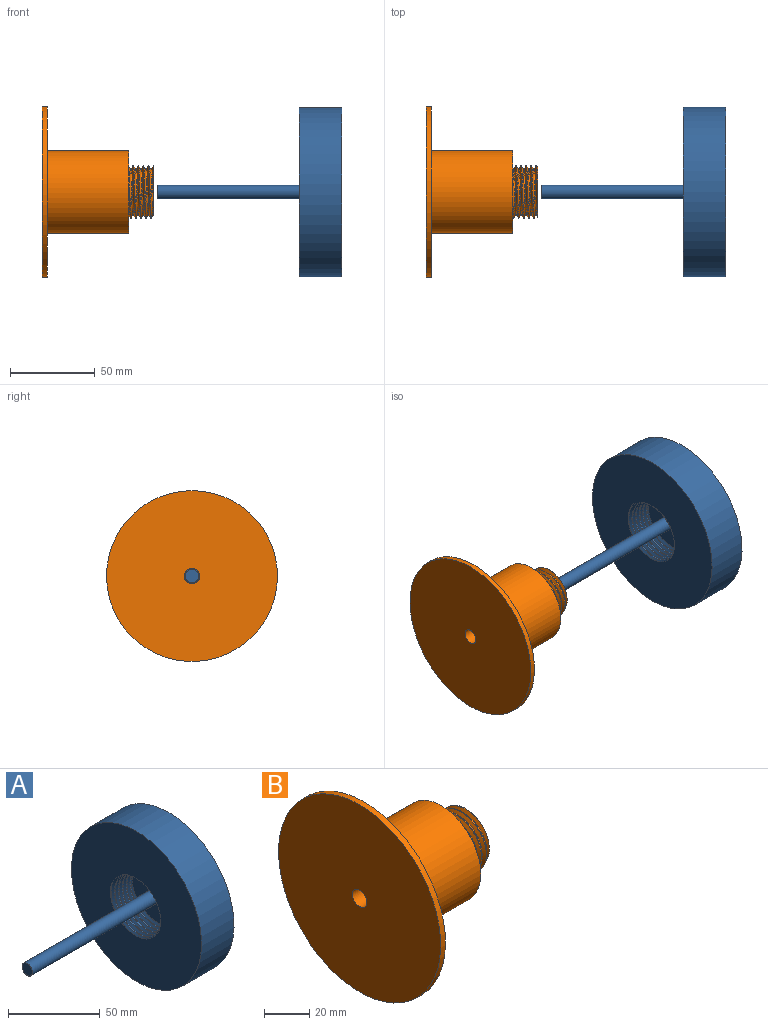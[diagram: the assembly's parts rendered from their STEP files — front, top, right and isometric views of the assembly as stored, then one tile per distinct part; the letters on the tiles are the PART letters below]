
ASSEMBLY  parts=2 mates=1
PART A: 10 faces, bbox 109.3x100.3x100.3 mm
  f0: plane 39.02x38.68mm, normal (-1,0,0), area 1111.3mm2, adj f5,f6,f7,f8,f9
  f1: plane 100.33x100.33mm, normal (-1,0,0), area 6692.4mm2, adj f4,f6,f7,f8,f9
  f2: plane 8x8mm, normal (-1,0,0), area 50.3mm2, adj f5
  f3: plane 100x100mm, normal (1,0,0), area 7854mm2, adj f4
  f4: cylinder r=50mm len=100mm, axis (-1,0,0), area 7854mm2, adj f1,f3
  f5: cylinder r=4mm len=100mm, axis (-1,0,0), area 2513.3mm2, adj f0,f2
  f6: bspline ~46.47x40.25mm, area 1214.5mm2, adj f0,f1,f8,f9
  f7: bspline ~46.47x40.25mm, area 1213.8mm2, adj f0,f1,f8,f9
  f8: bspline ~46.79x40.52mm, area 294mm2, adj f0,f1,f6,f7
  f9: cylinder r=18.5mm len=37mm, axis (1,0,0), area 450.2mm2, adj f0,f1,f6,f7
PART B: 11 faces, bbox 68x101.8x101.8 mm
  f0: cylinder r=15.5mm len=31mm, axis (-1,0,0), area 186.1mm2, adj f3,f4,f9,f10
  f1: plane 101x101mm, normal (-1,0,0), area 7948.2mm2, adj f2,f7
  f2: cylinder r=4.5mm len=66mm, axis (-1,0,0), area 1866.1mm2, adj f1,f3
  f3: plane 30.09x29.95mm, normal (1,0,0), area 603.6mm2, adj f0,f2,f8,f9,f10
  f4: plane 49.84x49.84mm, normal (1,0,0), area 1218.6mm2, adj f0,f5,f8,f9,f10
  f5: cylinder r=24.5mm len=49mm, axis (-1,0,0), area 7389mm2, adj f4,f6
  f6: plane 101x101mm, normal (1,0,0), area 6126.1mm2, adj f5,f7
  f7: cylinder r=50.5mm len=101mm, axis (-1,0,0), area 951.9mm2, adj f1,f6
  f8: bspline ~32.05x27.75mm, area 363.6mm2, adj f3,f4,f9,f10
  f9: bspline ~35.8x31mm, area 865.5mm2, adj f0,f3,f4,f8
  f10: bspline ~35.8x31mm, area 866mm2, adj f0,f3,f4,f8
PLACE A t=(-1.27,9.12,-9.03)mm
PLACE B t=(0.73,9.12,-9.03)mm fixed
MATE slider B.f0 <-> A.f4  axis (1,0,0) through (56.73,9.12,-9.03)mm
